# Revit family: 846911ARWNCL CARE 660 CF WFCC EH BE SF NCL
name_source: partatom
category: Plumbing Fixtures
revit_build: Autodesk Revit 2016 (Build: 20161004_0715(x64)
units: mm (PartAtom-declared; Revit-internal decimal feet)

## family parameters
Cut with Voids When Loaded = No
Host = Face
OmniClass Number = 23.45.05.21.11.11
OmniClass Title = Water Operated Water Closets
Part Type = Normal
Room Calculation Point = No
Round Connector Dimension = Use Diameter
Shared = No

## types (3) — shared parameters
ARH-Hole = No
ARH-Left = 1 mm  [stored 0.00328084 ft]
Assembly Code = D2010110
BI-Hole = No
BI-Void-Left = 1 mm  [stored 0.00328084 ft]
CW Connection = Yes
HW Connection = No
Manufacturer = GWA Bathrooms & Kitchens
Material_Arm = GWA_Metal-Stainless
Material_Buttons = GWA_Metal-Chrome
Material_Cistern = GWA-Porcelain-White
Material_Handle = GWA-Acrylic-White
Material_NC = GWA-Acrylic-Green
Material_Pan = GWA-Porcelain-White
Material_Seat_Mount = GWA_Metal-Stainless
URL = https://www.caroma.com.au
Vent Connection = No
Waste Connection = Yes
zero-valued in all types: ARH-Right, BI-Void-Right, Default Elevation

## per-type parameters (varying)
| type | Material_Seat | Model |
| CARE 660 CF WFCC EH BE SF NCL White | GWA-Acrylic-White | 846911ARWNCL |
| CARE 660 CF WFCC EH BE SF NCL Sorrento Blue | GWA-Acrylic-SB | 846911ARSBNCL |
| CARE 660 CF WFCC EH BE SF NCL Anthracite Grey | GWA-Acrylic-AG | 846911ARAGNCL |

note: column(s) folded — value = type name in every type: Description

note: [stored X ft] marks values corroborated as IEEE doubles in the binary element streams (Revit-internal decimal feet)

## geometry (parser evidence)
native form markers: Sweep x2
no freeform markers — native parametric forms only
